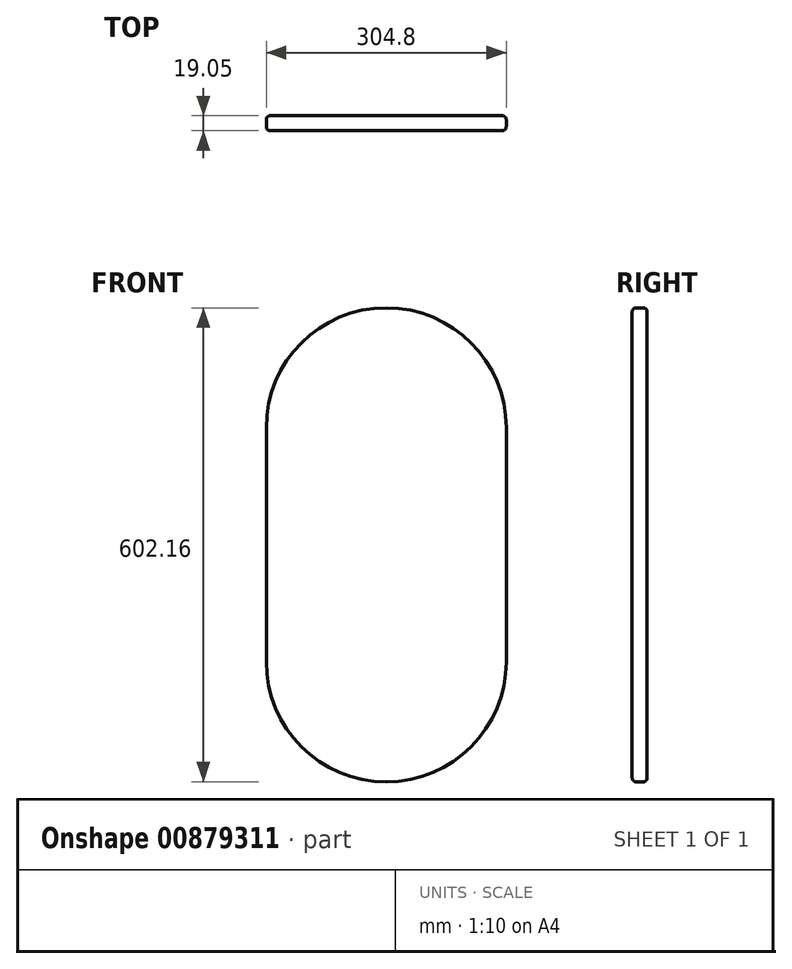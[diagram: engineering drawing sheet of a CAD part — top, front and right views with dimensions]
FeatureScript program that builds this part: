
annotation { "Feature Type Name" : "Feature", "Feature Type Description" : "" }
export const myFeature = defineFeature(function(context is Context, id is Id, definition is map)
    precondition{}
    {
        {
            var Q0;
            Q0=qCreatedBy(makeId("Front.planeOp"),FACE);
            var sketch = newSketch(context, id + "F0", { "sketchPlane" : qUnion([Q0])});
            skLineSegment(sketch, "E0", {"start": v(0, 0) * mm, "end": v(0, 457.2) * mm});
            skLineSegment(sketch, "E1", {"start": v(0, 457.2) * mm, "end": v(304.8, 457.2) * mm});
            skLineSegment(sketch, "E2", {"start": v(304.8, 457.2) * mm, "end": v(304.8, 0) * mm});
            skLineSegment(sketch, "E3", {"start": v(304.8, 0) * mm, "end": v(0, 0) * mm});
            skArc(sketch, "E4", {"start": v(304.8, 457.2) * mm, "mid": v(152.4, 609.6) * mm, "end": v(0, 457.2) * mm});
            skArc(sketch, "E5", {"start": v(304.8, 0) * mm, "mid": v(152.4, -152.4) * mm, "end": v(0, 0) * mm});
            skSolve(sketch);
        }
        {
            var Q0;
            Q0=makeQuery(id+"F0.imprint","IMPRINT",FACE,{"disambiguationData":[TD([[makeQuery(id+"F0.imprint","IMPRINT",EDGE,{"derivedFrom":sQuery(id+"F0.wireOp",EDGE,"E1")}),1.0]])]});
            var Q1;
            Q1=makeQuery(id+"F0.imprint","IMPRINT",FACE,{"disambiguationData":[TD([[makeQuery(id+"F0.imprint","IMPRINT",EDGE,{"derivedFrom":sQuery(id+"F0.wireOp",EDGE,"E0")}),-1.0]])]});
            var Q2;
            Q2=makeQuery(id+"F0.imprint","IMPRINT",FACE,{"disambiguationData":[TD([[makeQuery(id+"F0.imprint","IMPRINT",EDGE,{"derivedFrom":sQuery(id+"F0.wireOp",EDGE,"E3")}),1.0]])]});
            extrude(context, id + "F1", {"entities" : qUnion([Q0, Q1, Q2]), "depth" : 19.05 * mm, "offsetDistance" : 25.4 * mm});
        }
        {
            var Q0;
            Q0=makeQuery(id+"F1.opExtrude","CAP_EDGE",EDGE,{"disambiguationData":[OSD([sQuery(id+"F0.wireOp",EDGE,"E0")])],"isStart":false});
            var Q1;
            Q1=makeQuery(id+"F1.opExtrude","CAP_EDGE",EDGE,{"disambiguationData":[OSD([sQuery(id+"F0.wireOp",EDGE,"E4")])],"isStart":false});
            var Q2;
            Q2=makeQuery(id+"F1.opExtrude","CAP_EDGE",EDGE,{"disambiguationData":[OSD([sQuery(id+"F0.wireOp",EDGE,"E2")])],"isStart":false});
            var Q3;
            Q3=makeQuery(id+"F1.opExtrude","CAP_EDGE",EDGE,{"disambiguationData":[OSD([sQuery(id+"F0.wireOp",EDGE,"E5")])],"isStart":false});
            fillet(context, id + "F2", {"entities" : qUnion([Q0, Q1, Q2, Q3]), "radius" : 5.08 * mm, "tangentPropagation" : true, "allowEdgeOverflow" : false});
        }
        {
            var Q0;
            Q0=makeQuery(id+"F1.opExtrude","CAP_EDGE",EDGE,{"disambiguationData":[OSD([sQuery(id+"F0.wireOp",EDGE,"E2")])],"isStart":true});
            var Q1;
            Q1=makeQuery(id+"F1.opExtrude","CAP_EDGE",EDGE,{"disambiguationData":[OSD([sQuery(id+"F0.wireOp",EDGE,"E4")])],"isStart":true});
            var Q2;
            Q2=makeQuery(id+"F1.opExtrude","CAP_EDGE",EDGE,{"disambiguationData":[OSD([sQuery(id+"F0.wireOp",EDGE,"E0")])],"isStart":true});
            var Q3;
            Q3=makeQuery(id+"F1.opExtrude","CAP_EDGE",EDGE,{"disambiguationData":[OSD([sQuery(id+"F0.wireOp",EDGE,"E5")])],"isStart":true});
            fillet(context, id + "F3", {"entities" : qUnion([Q0, Q1, Q2, Q3]), "radius" : 5.08 * mm, "tangentPropagation" : true, "allowEdgeOverflow" : false});
        }
        {
            var Q0;
            Q0=qCreatedBy(makeId("Front.planeOp"),FACE);
            var sketch = newSketch(context, id + "F4", { "sketchPlane" : qUnion([Q0])});
            skLineSegment(sketch, "E6", {"start": v(0, 0) * mm, "end": v(0, 297.36) * mm});
            skLineSegment(sketch, "E7", {"start": v(0, 297.36) * mm, "end": v(304.8, 297.36) * mm});
            skLineSegment(sketch, "E8", {"start": v(304.8, 297.36) * mm, "end": v(304.8, 0) * mm});
            skLineSegment(sketch, "E9", {"start": v(304.8, 0) * mm, "end": v(0, 0) * mm});
            skArc(sketch, "E10", {"start": v(0, 297.36) * mm, "mid": v(152.4, 449.76) * mm, "end": v(304.8, 297.36) * mm});
            skArc(sketch, "E11", {"start": v(304.8, 0) * mm, "mid": v(152.4, -152.4) * mm, "end": v(0, 0) * mm});
            skSolve(sketch);
        }
        {
            var Q0;
            Q0=makeQuery(id+"F4.imprint","IMPRINT",FACE,{"disambiguationData":[TD([[makeQuery(id+"F4.imprint","IMPRINT",EDGE,{"derivedFrom":sQuery(id+"F4.wireOp",EDGE,"E6")}),-1.0]])]});
            var Q1;
            Q1=makeQuery(id+"F4.imprint","IMPRINT",FACE,{"disambiguationData":[TD([[makeQuery(id+"F4.imprint","IMPRINT",EDGE,{"derivedFrom":sQuery(id+"F4.wireOp",EDGE,"E7")}),1.0]])]});
            var Q2;
            Q2=makeQuery(id+"F4.imprint","IMPRINT",FACE,{"disambiguationData":[TD([[makeQuery(id+"F4.imprint","IMPRINT",EDGE,{"derivedFrom":sQuery(id+"F4.wireOp",EDGE,"E9")}),1.0]])]});
            extrude(context, id + "F5", {"entities" : qUnion([Q0, Q1, Q2]), "depth" : 19.05 * mm, "offsetDistance" : 25.4 * mm});
        }
        {
            var Q0;
            Q0=makeQuery(id+"F1.opExtrude","SWEPT_BODY",BODY,{"disambiguationData":[OSD([sQuery(id+"F0.wireOp",EDGE,"E0"),sQuery(id+"F0.wireOp",EDGE,"E2"),sQuery(id+"F0.wireOp",EDGE,"E4"),sQuery(id+"F0.wireOp",EDGE,"E5")])]});
            deleteBodies(context, id + "F6", {"entities" : qUnion([Q0])});
        }
        {
            var Q0;
            Q0=makeQuery(id+"F5.opExtrude","CAP_EDGE",EDGE,{"disambiguationData":[OSD([sQuery(id+"F4.wireOp",EDGE,"E6")])],"isStart":false});
            var Q1;
            Q1=makeQuery(id+"F5.opExtrude","CAP_EDGE",EDGE,{"disambiguationData":[OSD([sQuery(id+"F4.wireOp",EDGE,"E10")])],"isStart":false});
            var Q2;
            Q2=makeQuery(id+"F5.opExtrude","CAP_EDGE",EDGE,{"disambiguationData":[OSD([sQuery(id+"F4.wireOp",EDGE,"E8")])],"isStart":false});
            var Q3;
            Q3=makeQuery(id+"F5.opExtrude","CAP_EDGE",EDGE,{"disambiguationData":[OSD([sQuery(id+"F4.wireOp",EDGE,"E11")])],"isStart":false});
            fillet(context, id + "F7", {"entities" : qUnion([Q0, Q1, Q2, Q3]), "radius" : 5.08 * mm, "tangentPropagation" : true, "allowEdgeOverflow" : false});
        }
        {
            var Q0;
            Q0=makeQuery(id+"F5.opExtrude","CAP_EDGE",EDGE,{"disambiguationData":[OSD([sQuery(id+"F4.wireOp",EDGE,"E8")])],"isStart":true});
            var Q1;
            Q1=makeQuery(id+"F5.opExtrude","CAP_EDGE",EDGE,{"disambiguationData":[OSD([sQuery(id+"F4.wireOp",EDGE,"E10")])],"isStart":true});
            var Q2;
            Q2=makeQuery(id+"F5.opExtrude","CAP_EDGE",EDGE,{"disambiguationData":[OSD([sQuery(id+"F4.wireOp",EDGE,"E6")])],"isStart":true});
            var Q3;
            Q3=makeQuery(id+"F5.opExtrude","CAP_EDGE",EDGE,{"disambiguationData":[OSD([sQuery(id+"F4.wireOp",EDGE,"E11")])],"isStart":true});
            fillet(context, id + "F8", {"entities" : qUnion([Q0, Q1, Q2, Q3]), "radius" : 5.08 * mm, "tangentPropagation" : true, "allowEdgeOverflow" : false});
        }
    });
